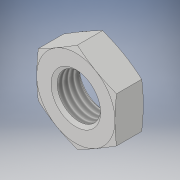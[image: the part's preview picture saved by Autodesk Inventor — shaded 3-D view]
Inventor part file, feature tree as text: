
AUTODESK INVENTOR PART (.ipt)
format: ipt  version: 2019 (Build 230136000, 136)  size: 179,712 bytes
history: native  units: in
note: dims shown in document units (in); Inventor stores cm internally (conversion verified against a paired STEP export)
features: other x70, sketch x3, revolve x2, extrude x1, thread x1
ambient origin geometry x8: Origin, YZ Plane, XZ Plane, XY Plane, X Axis, Y Axis, Z Axis, Center Point
bodies: Solid1 (feature_tree)
feature tree (77):
  sketch  "Sketch_8"  dims[d0=360.0deg d1=0.25in d2=0.0in]
  sketch  "Sketch_10"  dims[d3=360.0deg d4=0.1959in d5=0.0in]
  revolve  "Revolution1"  [1 undecoded]
  extrude  "Extrusion1"  Depth=0.1959in TaperAngle=0.0deg
  revolve  "Revolution2"  [1 undecoded]
  thread  "Thread1"  [1 undecoded]
  other  "NUT_XY"
  other  "NUT_YZ"
  other  "NUT_ZX"
  other  "NUT_X"
  other  "NUT_Y"
  other  "NUT_Z"
  other  "NUT_Center"
  other  "a1_XY"
  other  "a1_YZ"
  other  "a1_ZX"
  other  "a1_X"
  other  "a1_Y"
  other  "a1_Z"
  other  "a1_Center"
  other  "a2_XY"
  other  "a2_YZ"
  other  "a2_ZX"
  other  "a2_X"
  other  "a2_Y"
  other  "a2_Z"
  other  "a2_Center"
  other  "b1_XY"
  other  "b1_YZ"
  other  "b1_ZX"
  other  "b1_X"
  other  "b1_Y"
  other  "b1_Z"
  other  "b1_Center"
  other  "b2_XY"
  other  "b2_YZ"
  other  "b2_ZX"
  other  "b2_X"
  other  "b2_Y"
  other  "b2_Z"
  other  "b2_Center"
  other  "e_XY"
  other  "e_YZ"
  other  "e_ZX"
  other  "e_X"
  other  "e_Y"
  other  "e_Z"
  other  "e_Center"
  other  "ol1_XY"
  other  "ol1_YZ"
  other  "ol1_ZX"
  other  "ol1_X"
  other  "ol1_Y"
  other  "ol1_Z"
  other  "ol1_Center"
  other  "ol2_XY"
  other  "ol2_YZ"
  other  "ol2_ZX"
  other  "ol2_X"
  other  "ol2_Y"
  other  "ol2_Z"
  other  "ol2_Center"
  other  "th1_XY"
  other  "th1_YZ"
  other  "th1_ZX"
  other  "th1_X"
  other  "th1_Y"
  other  "th1_Z"
  other  "th1_Center"
  other  "th2_XY"
  other  "th2_YZ"
  other  "th2_ZX"
  other  "th2_X"
  other  "th2_Y"
  other  "th2_Z"
  other  "th2_Center"
  sketch  "Sketch_11"  dims[d6=0.0in d7=0.0in d8=0.0in]
note: 3 required parameter values undecoded (feature->parameter linkage not recoverable at this tier; creation-order binding heuristic only, values carry confidence <= 0.55)